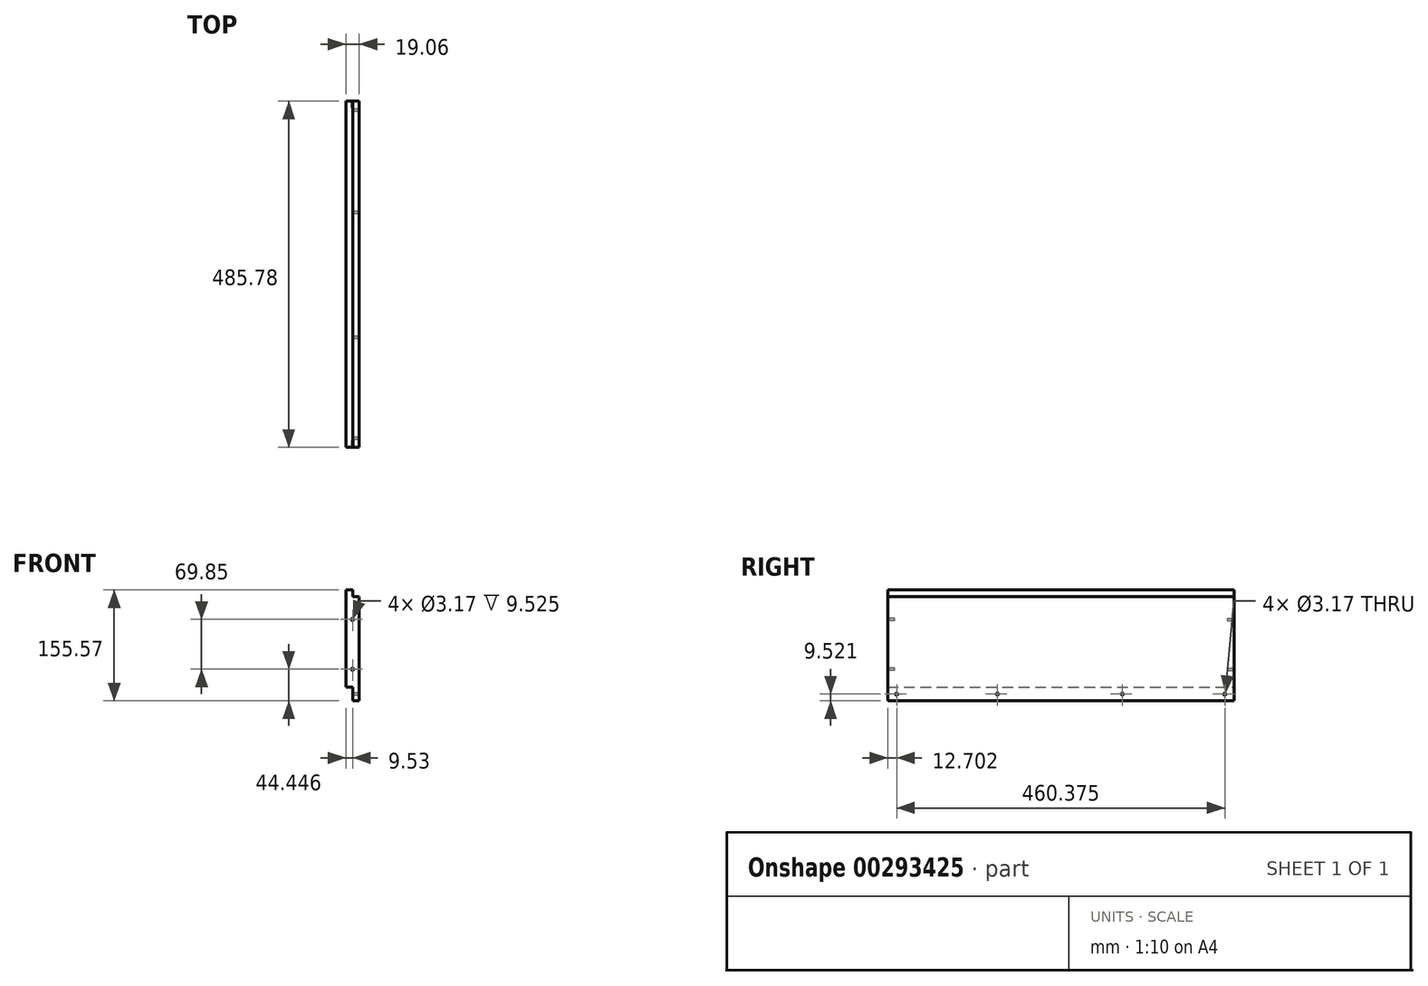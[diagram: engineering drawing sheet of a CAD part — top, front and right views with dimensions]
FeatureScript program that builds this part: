
annotation { "Feature Type Name" : "Feature", "Feature Type Description" : "" }
export const myFeature = defineFeature(function(context is Context, id is Id, definition is map)
    precondition{}
    {
        {
            var Q0;
            Q0=qCreatedBy(makeId("Right.planeOp"),FACE);
            var sketch = newSketch(context, id + "F0", { "sketchPlane" : qUnion([Q0])});
            skLineSegment(sketch, "E0.bottom", {"start": v(242.89, 216.38) * mm, "end": v(-242.89, 216.38) * mm});
            skLineSegment(sketch, "E0.top", {"start": v(242.89, -158.27) * mm, "end": v(-242.89, -158.27) * mm});
            skLineSegment(sketch, "E0.left", {"start": v(242.89, 216.38) * mm, "end": v(242.89, -158.27) * mm});
            skLineSegment(sketch, "E0.right", {"start": v(-242.89, 216.38) * mm, "end": v(-242.89, -158.27) * mm});
            skPoint(sketch, "E0.middle", {"position": v(0, 29.05) * mm});
            skLineSegment(sketch, "E1.bottom", {"start": v(-242.89, 216.38) * mm, "end": v(242.89, 216.38) * mm});
            skLineSegment(sketch, "E1.top", {"start": v(-242.89, -139.22) * mm, "end": v(242.89, -139.22) * mm});
            skLineSegment(sketch, "E1.left", {"start": v(-242.89, 216.38) * mm, "end": v(-242.89, -139.22) * mm});
            skLineSegment(sketch, "E1.right", {"start": v(242.89, 216.38) * mm, "end": v(242.89, -139.22) * mm});
            skLineSegment(sketch, "E2.bottom", {"start": v(252.41, 216.38) * mm, "end": v(-252.41, 216.38) * mm, "construction": true});
            skLineSegment(sketch, "E2.top", {"start": v(252.41, -158.27) * mm, "end": v(-252.41, -158.27) * mm, "construction": true});
            skLineSegment(sketch, "E2.left", {"start": v(252.41, 216.38) * mm, "end": v(252.41, -158.27) * mm, "construction": true});
            skLineSegment(sketch, "E2.right", {"start": v(-252.41, 216.38) * mm, "end": v(-252.41, -158.27) * mm, "construction": true});
            skLineSegment(sketch, "E3", {"start": v(-242.89, -12.22) * mm, "end": v(242.89, -12.22) * mm});
            skLineSegment(sketch, "E4", {"start": v(242.89, -2.7) * mm, "end": v(-242.89, -2.7) * mm});
            skLineSegment(sketch, "E5.bottom", {"start": v(50.8, -101.12) * mm, "end": v(-50.8, -101.12) * mm});
            skLineSegment(sketch, "E5.top", {"start": v(50.8, -113.82) * mm, "end": v(-50.8, -113.82) * mm});
            skArc(sketch, "E6", {"start": v(50.8, -113.82) * mm, "mid": v(57.15, -107.47) * mm, "end": v(50.8, -101.12) * mm});
            skArc(sketch, "E7", {"start": v(-50.8, -101.12) * mm, "mid": v(-57.15, -107.47) * mm, "end": v(-50.8, -113.82) * mm});
            skCircle(sketch, "E8", {"center": v(-230.19, -148.75) * mm, "radius": 1.59 * mm});
            skCircle(sketch, "E9", {"center": v(230.19, -148.75) * mm, "radius": 1.59 * mm});
            skCircle(sketch, "E10", {"center": v(-88.9, -148.75) * mm, "radius": 1.59 * mm});
            skCircle(sketch, "E11", {"center": v(86.36, -148.75) * mm, "radius": 1.59 * mm});
            skSolve(sketch);
        }
        {
            var Q0;
            Q0=makeQuery(id+"F0.imprint","IMPRINT",FACE,{"disambiguationData":[TD([[makeQuery(id+"F0.imprint","IMPRINT",EDGE,{"derivedFrom":sQuery(id+"F0.wireOp",EDGE,"E0.top")}),-1.0]])]});
            var Q1;
            {var subQ2=sQuery(id+"F0.wireOp",EDGE,"E1.top");Q1=makeQuery(id+"F0.imprint","IMPRINT",FACE,{"disambiguationData":[TD([[makeQuery(id+"F0.imprint","IMPRINT",EDGE,{"derivedFrom":subQ2}),1.0]])]});}
            var Q2;
            Q2=makeQuery(id+"F0.imprint","IMPRINT",FACE,{"disambiguationData":[TD([[makeQuery(id+"F0.imprint","IMPRINT",EDGE,{"derivedFrom":sQuery(id+"F0.wireOp",EDGE,"E5.bottom")}),1.0]])]});
            extrude(context, id + "F1", {"entities" : qUnion([Q0, Q1, Q2]), "depth" : 9.52 * mm});
        }
        {
            var Q0;
            {var subQ2=sQuery(id+"F0.wireOp",EDGE,"E1.top");Q0=makeQuery(id+"F0.imprint","IMPRINT",FACE,{"disambiguationData":[TD([[makeQuery(id+"F0.imprint","IMPRINT",EDGE,{"derivedFrom":subQ2}),1.0]])]});}
            var Q1;
            {var subQ0=sQuery(id+"F0.wireOp",EDGE,"E3");Q1=makeQuery(id+"F0.imprint","IMPRINT",FACE,{"disambiguationData":[TD([[makeQuery(id+"F0.imprint","IMPRINT",EDGE,{"derivedFrom":subQ0}),1.0]])]});}
            var Q2;
            Q2=makeQuery(id+"F0.imprint","IMPRINT",FACE,{"disambiguationData":[TD([[makeQuery(id+"F0.imprint","IMPRINT",EDGE,{"derivedFrom":sQuery(id+"F0.wireOp",EDGE,"E5.bottom")}),1.0]])]});
            extrude(context, id + "F2", {"entities" : qUnion([Q0, Q1, Q2]), "operationType" : NewBodyOperationType.ADD, "oppositeDirection" : true, "depth" : 9.52 * mm});
        }
        {
            var Q0;
            {var subQ0=sQuery(id+"F0.wireOp",EDGE,"E1.left");Q0=makeQuery(id+"F2.boolean.opBoolean","MERGE",FACE,{"derivedFrom":[makeQuery(id+"F1.opExtrude","SWEPT_FACE",FACE,{"disambiguationData":[OSD([sQuery(id+"F0.wireOp",EDGE,"E0.right"),subQ0])]}),makeQuery(id+"F2.opExtrude","SWEPT_FACE",FACE,{"disambiguationData":[OSD([subQ0])]})]});}
            var sketch = newSketch(context, id + "F3", { "sketchPlane" : qUnion([Q0])});
            skCircle(sketch, "E12", {"center": v(0, -113.82) * mm, "radius": 1.59 * mm});
            skCircle(sketch, "E13", {"center": v(0, -43.97) * mm, "radius": 1.59 * mm});
            skSolve(sketch);
        }
        {
            var Q0;
            {var subQ0=sQuery(id+"F0.wireOp",EDGE,"E1.right");Q0=makeQuery(id+"F2.boolean.opBoolean","MERGE",FACE,{"derivedFrom":[makeQuery(id+"F1.opExtrude","SWEPT_FACE",FACE,{"disambiguationData":[OSD([sQuery(id+"F0.wireOp",EDGE,"E0.left"),subQ0])]}),makeQuery(id+"F2.opExtrude","SWEPT_FACE",FACE,{"disambiguationData":[OSD([subQ0])]})]});}
            var sketch = newSketch(context, id + "F4", { "sketchPlane" : qUnion([Q0])});
            skCircle(sketch, "E14", {"center": v(0, -113.82) * mm, "radius": 1.59 * mm});
            skCircle(sketch, "E15", {"center": v(0, -43.97) * mm, "radius": 1.59 * mm});
            skSolve(sketch);
        }
        {
            var Q0;
            Q0=makeQuery(id+"F4.imprint","IMPRINT",FACE,{"disambiguationData":[TD([[makeQuery(id+"F4.imprint","IMPRINT",EDGE,{"derivedFrom":sQuery(id+"F4.wireOp",EDGE,"E15")}),1.0]])]});
            var Q1;
            Q1=makeQuery(id+"F4.imprint","IMPRINT",FACE,{"disambiguationData":[TD([[makeQuery(id+"F4.imprint","IMPRINT",EDGE,{"derivedFrom":sQuery(id+"F4.wireOp",EDGE,"E14")}),1.0]])]});
            extrude(context, id + "F5", {"entities" : qUnion([Q0, Q1]), "operationType" : NewBodyOperationType.REMOVE, "oppositeDirection" : true, "depth" : 9.52 * mm});
        }
        {
            var Q0;
            Q0=makeQuery(id+"F3.imprint","IMPRINT",FACE,{"disambiguationData":[TD([[makeQuery(id+"F3.imprint","IMPRINT",EDGE,{"derivedFrom":sQuery(id+"F3.wireOp",EDGE,"E12")}),1.0]])]});
            var Q1;
            Q1=makeQuery(id+"F3.imprint","IMPRINT",FACE,{"disambiguationData":[TD([[makeQuery(id+"F3.imprint","IMPRINT",EDGE,{"derivedFrom":sQuery(id+"F3.wireOp",EDGE,"E13")}),1.0]])]});
            extrude(context, id + "F6", {"entities" : qUnion([Q0, Q1]), "operationType" : NewBodyOperationType.REMOVE, "oppositeDirection" : true, "depth" : 9.52 * mm});
        }
    });
